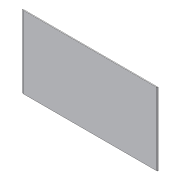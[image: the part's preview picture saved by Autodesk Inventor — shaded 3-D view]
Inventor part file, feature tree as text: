
AUTODESK INVENTOR PART (.ipt)
format: ipt  version: 2012 (Build 160160000, 160)  size: 75,264 bytes
history: native  units: in
note: dims shown in document units (in); Inventor stores cm internally (conversion verified against a paired STEP export)
features: chamfer x2, extrude x1, sketch x1
ambient origin geometry x8: Origin, YZ Plane, XZ Plane, XY Plane, X Axis, Y Axis, Z Axis, Center Point
bodies: Solid1 (feature_tree)
feature tree (4):
  extrude  "Extrusion1"  Depth=88.0in
  chamfer  "Chamfer1"  Distance=0.5in
  chamfer  "Chamfer3"  Distance=0.25in Angle=75.0deg
  sketch  "Sketch1"  dims[d0=47.0in d1=88.0in d2=0.5in d3=0.0in d4=0.25in d5=0.125in d6=75.0deg d10=0.25in d11=0.125in d12=75.0deg]
